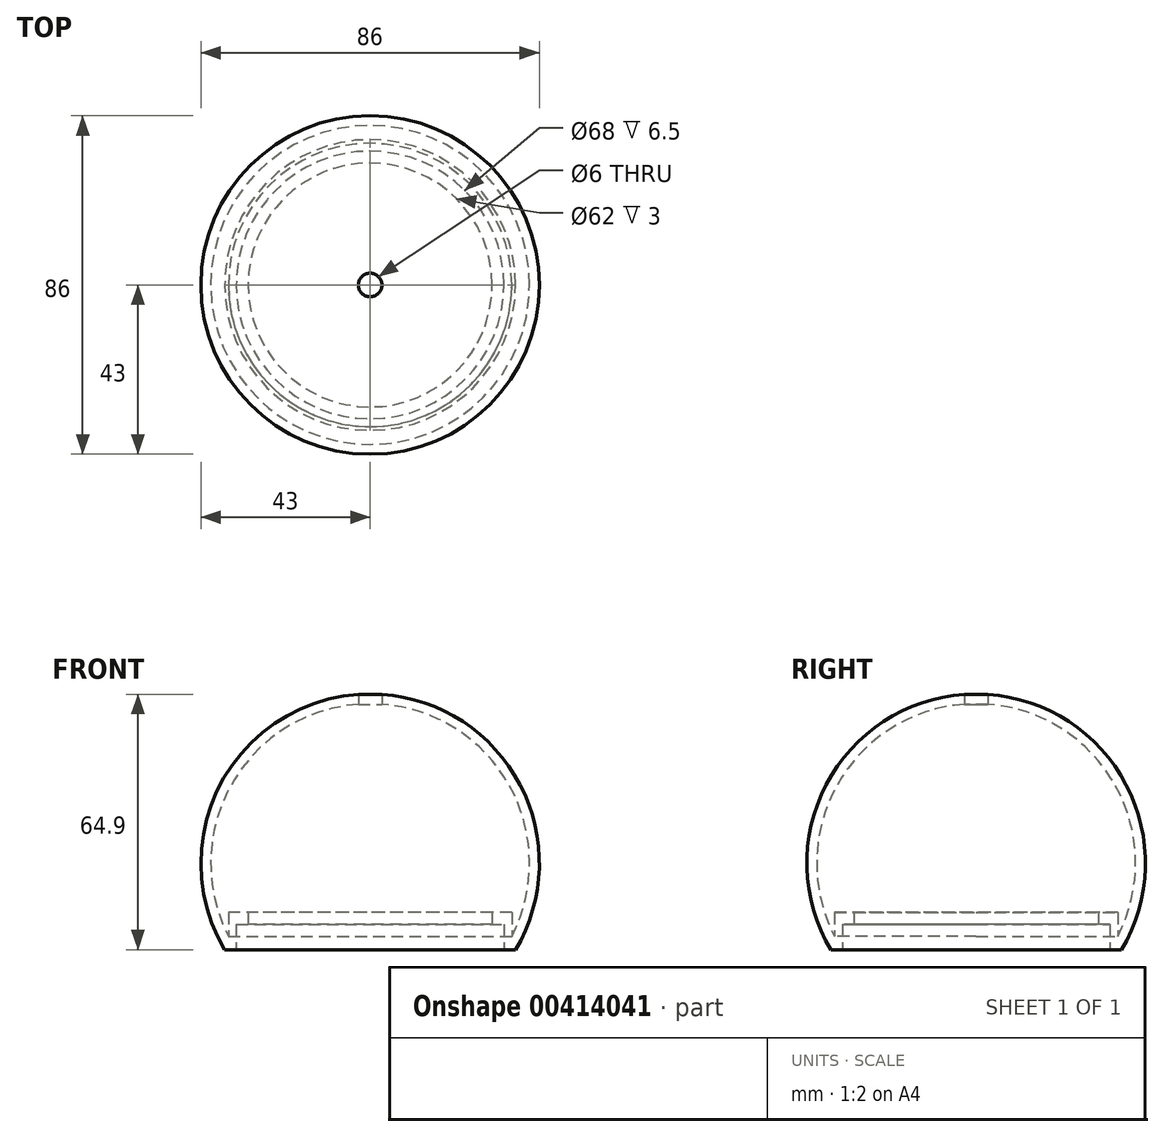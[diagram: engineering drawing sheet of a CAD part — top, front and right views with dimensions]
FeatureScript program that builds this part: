
annotation { "Feature Type Name" : "Feature", "Feature Type Description" : "" }
export const myFeature = defineFeature(function(context is Context, id is Id, definition is map)
    precondition{}
    {
        {
            var Q0;
            Q0=qCreatedBy(makeId("Front.planeOp"),FACE);
            var sketch = newSketch(context, id + "F0", { "sketchPlane" : qUnion([Q0])});
            skArc(sketch, "E0", {"start": v(0, 65) * mm, "mid": v(-37.38, 43.25) * mm, "end": v(-36.95, 0) * mm});
            skLineSegment(sketch, "E1", {"start": v(0, -45.76) * mm, "end": v(0, 86.4) * mm, "construction": true});
            skLineSegment(sketch, "E2", {"start": v(35.1, 0) * mm, "end": v(-50.8, 0) * mm});
            skLineSegment(sketch, "E3", {"start": v(0, 65) * mm, "end": v(0, 0) * mm});
            skSolve(sketch);
        }
        {
            var Q0;
            Q0 = qSketchRegion(id + "F0", true);
            var Q1;
            Q1=sQuery(id+"F0.wireOp",EDGE,"E1");
            revolve(context, id + "F1", {"entities" : qUnion([Q0]), "axis" : qUnion([Q1]), "revolveType" : RevolveType.FULL});
        }
        {
            var Q0;
            Q0=makeQuery(id+"F1.opRevolve","SWEPT_FACE",FACE,{"disambiguationData":[OSD([sQuery(id+"F0.wireOp",EDGE,"E0")])]});
            var Q1;
            Q1=makeQuery(id+"F1.opRevolve","SWEPT_BODY",BODY,{"disambiguationData":[OSD([sQuery(id+"F0.wireOp",EDGE,"E0"),sQuery(id+"F0.wireOp",EDGE,"E2"),sQuery(id+"F0.wireOp",EDGE,"E3")])]});
            shell(context, id + "F2", {"isHollow" : true, "entities" : qUnion([Q0]), "parts" : qUnion([Q1]), "thickness" : 2.5 * mm});
        }
        {
            var Q0;
            Q0=makeQuery(id+"F1.opRevolve","SWEPT_FACE",FACE,{"disambiguationData":[OSD([sQuery(id+"F0.wireOp",EDGE,"E2")])]});
            var sketch = newSketch(context, id + "F3", { "sketchPlane" : qUnion([Q0])});
            skCircle(sketch, "E4", {"center": v(0, 0) * mm, "radius": 34 * mm});
            skSolve(sketch);
        }
        {
            var Q0;
            Q0 = qSketchRegion(id + "F3", true);
            extrude(context, id + "F4", {"entities" : qUnion([Q0]), "operationType" : NewBodyOperationType.REMOVE, "oppositeDirection" : true, "depth" : 4.2 * mm});
        }
        {
            var Q0;
            Q0=qCreatedBy(makeId("Top.planeOp"),FACE);
            cPlane(context, id + "F5", {"entities" : qUnion([Q0]), "cplaneType" : CPlaneType.OFFSET, "offset" : 52 * mm, "width" : 150 * mm, "height" : 150 * mm});
        }
        {
            var Q0;
            Q0=qCreatedBy(id+"F5.planeOp",FACE);
            var sketch = newSketch(context, id + "F6", { "sketchPlane" : qUnion([Q0])});
            skCircle(sketch, "E5", {"center": v(0, 0) * mm, "radius": 3 * mm});
            skSolve(sketch);
        }
        {
            var Q0;
            Q0 = qSketchRegion(id + "F6", true);
            extrude(context, id + "F7", {"entities" : qUnion([Q0]), "operationType" : NewBodyOperationType.REMOVE, "depth" : 14 * mm});
        }
        {
            var Q0;
            Q0=makeQuery(id+"F2.opShell","OFFSET_FACE",FACE,{"disambiguationData":[OSD([sQuery(id+"F0.wireOp",EDGE,"E2")])]});
            var sketch = newSketch(context, id + "F8", { "sketchPlane" : qUnion([Q0])});
            skCircle(sketch, "E6.0", {"center": v(0, 0) * mm, "radius": 34 * mm});
            skCircle(sketch, "E7.0", {"center": v(0, 0) * mm, "radius": 36 * mm});
            skSolve(sketch);
        }
        {
            var Q0;
            Q0 = qSketchRegion(id + "F8", true);
            extrude(context, id + "F9", {"entities" : qUnion([Q0]), "operationType" : NewBodyOperationType.ADD, "depth" : 4 * mm});
        }
        {
            var Q0;
            Q0=makeQuery(id+"F9.opExtrude","CAP_FACE",FACE,{"disambiguationData":[OSD([sQuery(id+"F8.wireOp",EDGE,"E6.0"),sQuery(id+"F8.wireOp",EDGE,"E7.0")])],"isStart":false});
            var sketch = newSketch(context, id + "F10", { "sketchPlane" : qUnion([Q0])});
            skCircle(sketch, "E8.0", {"center": v(0, 0) * mm, "radius": 36 * mm});
            skCircle(sketch, "E9.0", {"center": v(0, 0) * mm, "radius": 31 * mm});
            skSolve(sketch);
        }
        {
            var Q0;
            Q0 = qSketchRegion(id + "F10", true);
            extrude(context, id + "F11", {"entities" : qUnion([Q0]), "operationType" : NewBodyOperationType.ADD, "depth" : 3 * mm});
        }
    });
